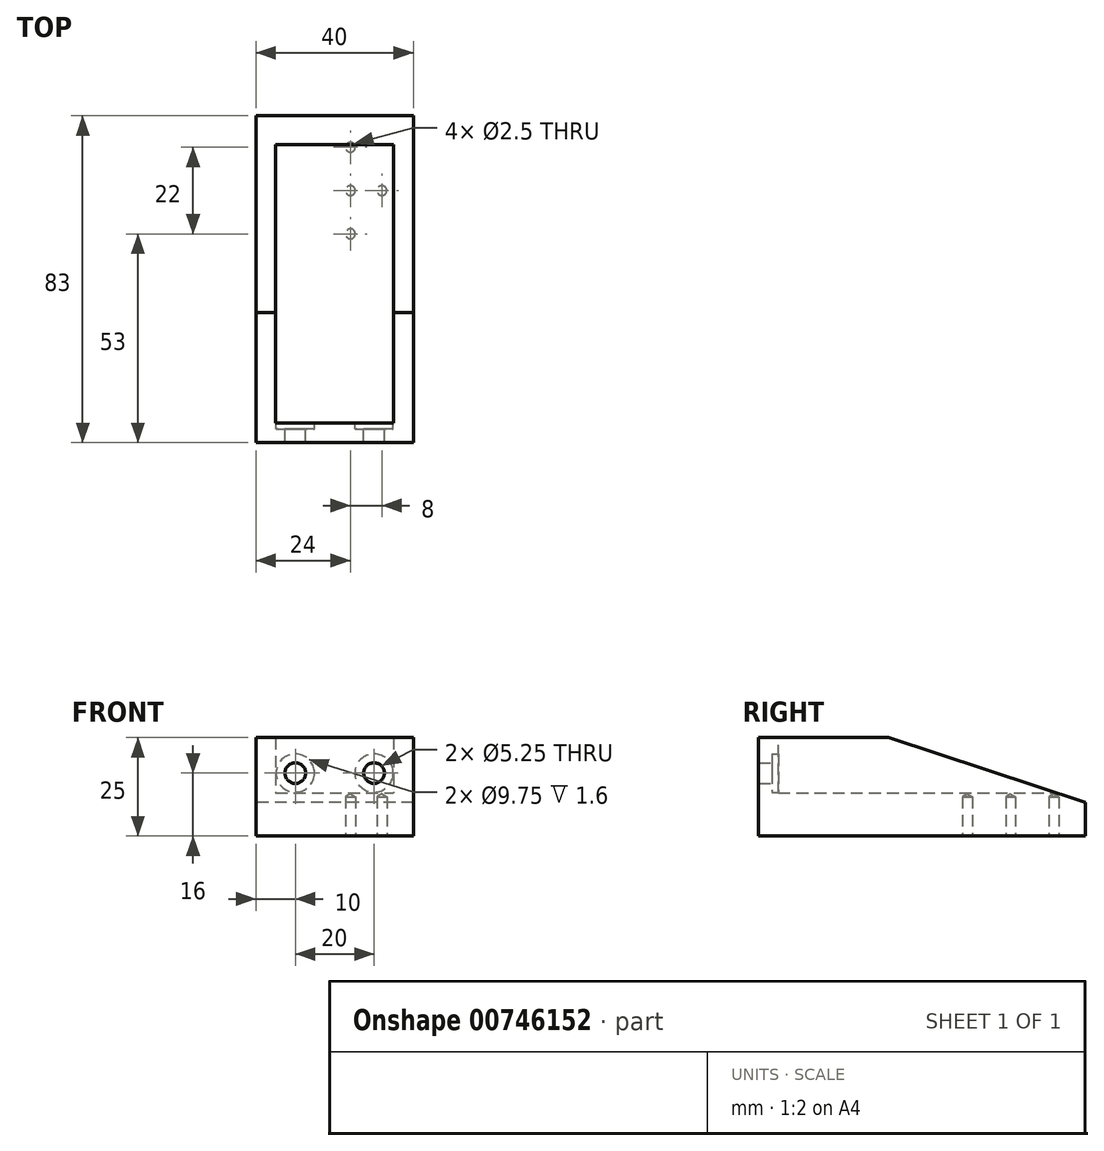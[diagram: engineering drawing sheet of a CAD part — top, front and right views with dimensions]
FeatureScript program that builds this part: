
annotation { "Feature Type Name" : "Feature", "Feature Type Description" : "" }
export const myFeature = defineFeature(function(context is Context, id is Id, definition is map)
    precondition{}
    {
        {
            var Q0;
            Q0=qCreatedBy(makeId("Right.planeOp"),FACE);
            var sketch = newSketch(context, id + "F0", { "sketchPlane" : qUnion([Q0])});
            skLineSegment(sketch, "E0", {"start": v(-78, 0) * mm, "end": v(-78, 16.5) * mm});
            skLineSegment(sketch, "E1", {"start": v(-78, 16.5) * mm, "end": v(-83, 16.5) * mm});
            skLineSegment(sketch, "E2", {"start": v(-83, 16.5) * mm, "end": v(-83, -8.5) * mm});
            skLineSegment(sketch, "E3", {"start": v(-83, -8.5) * mm, "end": v(0, -8.5) * mm});
            skLineSegment(sketch, "E4", {"start": v(0, -8.5) * mm, "end": v(0, 0) * mm});
            skLineSegment(sketch, "E5", {"start": v(0, 0) * mm, "end": v(-78, 0) * mm});
            skLineSegment(sketch, "E6", {"start": v(-78, 16.5) * mm, "end": v(-50, 16.5) * mm});
            skLineSegment(sketch, "E7", {"start": v(-50, 16.5) * mm, "end": v(0, 0) * mm});
            skSolve(sketch);
        }
        {
            var Q0;
            Q0=makeQuery(id+"F0.imprint","IMPRINT",FACE,{"disambiguationData":[TD([[makeQuery(id+"F0.imprint","IMPRINT",EDGE,{"derivedFrom":sQuery(id+"F0.wireOp",EDGE,"E0")}),1.0]])]});
            var Q1;
            {var subQ0=sQuery(id+"F0.wireOp",EDGE,"H235q9Pv-cFfw-opsN-Odyi-TBDRe71CPrCy");Q1=makeQuery(id+"F0.imprint","IMPRINT",FACE,{"disambiguationData":[TD([[makeQuery(id+"F0.imprint","IMPRINT",EDGE,{"derivedFrom":subQ0}),1.0]])]});}
            var Q2;
            Q2=makeQuery(id+"F0.imprint","IMPRINT",FACE,{"disambiguationData":[TD([[makeQuery(id+"F0.imprint","IMPRINT",EDGE,{"derivedFrom":sQuery(id+"F0.wireOp",EDGE,"E0")}),-1.0]])]});
            extrude(context, id + "F1", {"entities" : qUnion([Q0, Q1, Q2]), "depth" : 40 * mm, "offsetDistance" : 25 * mm});
        }
        {
            var Q0;
            Q0=makeQuery(id+"F1.opExtrude","SWEPT_FACE",FACE,{"disambiguationData":[OSD([sQuery(id+"F0.wireOp",EDGE,"E3")])]});
            var sketch = newSketch(context, id + "F2", { "sketchPlane" : qUnion([Q0])});
            skPoint(sketch, "E8", {"position": v(24, 8) * mm});
            skPoint(sketch, "E9", {"position": v(24, 19) * mm});
            skPoint(sketch, "E10", {"position": v(24, 30) * mm});
            skPoint(sketch, "E11", {"position": v(32, 19) * mm});
            skLineSegment(sketch, "E12", {"start": v(32, 83) * mm, "end": v(32, 0) * mm, "construction": true});
            skLineSegment(sketch, "E13", {"start": v(24, 0) * mm, "end": v(24, 83) * mm, "construction": true});
            skLineSegment(sketch, "E14", {"start": v(32, 19) * mm, "end": v(24, 19) * mm});
            skLineSegment(sketch, "E15", {"start": v(24, 8) * mm, "end": v(32, 19) * mm});
            skLineSegment(sketch, "E16", {"start": v(24, 30) * mm, "end": v(32, 19) * mm});
            skLineSegment(sketch, "E17", {"start": v(24, 19) * mm, "end": v(24, 30) * mm});
            skLineSegment(sketch, "E18", {"start": v(24, 19) * mm, "end": v(24, 8) * mm});
            skSolve(sketch);
        }
        {
            var Q0;
            Q0=makeQuery(id+"F1.opExtrude","SWEPT_FACE",FACE,{"disambiguationData":[OSD([sQuery(id+"F0.wireOp",EDGE,"E1"),sQuery(id+"F0.wireOp",EDGE,"E6")])]});
            var sketch = newSketch(context, id + "F3", { "sketchPlane" : qUnion([Q0])});
            skLineSegment(sketch, "E19.bottom", {"start": v(35, -78) * mm, "end": v(5, -78) * mm});
            skLineSegment(sketch, "E19.top", {"start": v(35, -5) * mm, "end": v(5, -5) * mm});
            skLineSegment(sketch, "E19.left", {"start": v(35, -78) * mm, "end": v(35, -5) * mm});
            skLineSegment(sketch, "E19.right", {"start": v(5, -78) * mm, "end": v(5, -5) * mm});
            skSolve(sketch);
        }
        {
            var Q0;
            {var subQ0=sQuery(id+"F3.wireOp",EDGE,"E19.bottom");Q0=makeQuery(id+"F3.imprint","IMPRINT",FACE,{"disambiguationData":[TD([[makeQuery(id+"F3.imprint","IMPRINT",EDGE,{"derivedFrom":subQ0}),-1.0]])]});}
            var Q1;
            {var subQ0=sQuery(id+"F3.wireOp",EDGE,"E19.top");Q1=makeQuery(id+"F3.imprint","IMPRINT",FACE,{"disambiguationData":[TD([[makeQuery(id+"F3.imprint","IMPRINT",EDGE,{"derivedFrom":subQ0}),1.0]])]});}
            extrude(context, id + "F4", {"entities" : qUnion([Q0, Q1]), "operationType" : NewBodyOperationType.REMOVE, "oppositeDirection" : true, "depth" : 14.1 * mm, "offsetDistance" : 25 * mm});
        }
        {
            var Q0;
            Q0=makeQuery(id+"F4.boolean.opBoolean","COPY",FACE,{"derivedFrom":makeQuery(id+"F4.opExtrude","SWEPT_FACE",FACE,{"disambiguationData":[OSD([sQuery(id+"F3.wireOp",EDGE,"E19.bottom")])]})});
            var sketch = newSketch(context, id + "F5", { "sketchPlane" : qUnion([Q0])});
            skPoint(sketch, "E20", {"position": v(-30, 7.5) * mm});
            skPoint(sketch, "E21", {"position": v(-10, 7.5) * mm});
            skSolve(sketch);
        }
        {
            var Q0;
            Q0=sQuery(id+"F5.wireOp",VERTEX,"E20");
            var Q1;
            Q1=sQuery(id+"F5.wireOp",VERTEX,"E21");
            var Q2;
            Q2=makeQuery(id+"F1.opExtrude","SWEPT_BODY",BODY,{"disambiguationData":[OSD([sQuery(id+"F0.wireOp",EDGE,"E1"),sQuery(id+"F0.wireOp",EDGE,"E2"),sQuery(id+"F0.wireOp",EDGE,"E3"),sQuery(id+"F0.wireOp",EDGE,"E4"),sQuery(id+"F0.wireOp",EDGE,"E6"),sQuery(id+"F0.wireOp",EDGE,"E7")])]});
            hole(context, id + "F6", {"style" : HoleStyle.C_BORE, "endStyle" : HoleEndStyle.BLIND, "holeDiameter" : 5.25 * mm, "cBoreDiameter" : 9.75 * mm, "cBoreDepth" : 1.6 * mm, "majorDiameter" : 5 * mm, "holeDepth" : 5 * mm, "isTappedThrough" : true, "tappedDepth" : 12 * mm, "tapClearance" : 3, "startFromSketch" : true, "locations" : qUnion([Q0, Q1]), "scope" : qUnion([Q2])});
        }
        {
            var Q0;
            Q0=sQuery(id+"F2.wireOp",VERTEX,"E10");
            var Q1;
            Q1=sQuery(id+"F2.wireOp",VERTEX,"E9");
            var Q2;
            Q2=sQuery(id+"F2.wireOp",VERTEX,"E14.start");
            var Q3;
            Q3=sQuery(id+"F2.wireOp",VERTEX,"E8");
            var Q4;
            Q4=makeQuery(id+"F1.opExtrude","SWEPT_BODY",BODY,{"disambiguationData":[OSD([sQuery(id+"F0.wireOp",EDGE,"E1"),sQuery(id+"F0.wireOp",EDGE,"E2"),sQuery(id+"F0.wireOp",EDGE,"E3"),sQuery(id+"F0.wireOp",EDGE,"E4"),sQuery(id+"F0.wireOp",EDGE,"E6"),sQuery(id+"F0.wireOp",EDGE,"E7")])]});
            hole(context, id + "F7", {"style" : HoleStyle.SIMPLE, "endStyle" : HoleEndStyle.BLIND, "standardTappedOrClearance" : lookupTablePath({ "standard" : "ISO", "engagement" : "75%", "pitch" : "0.5 mm", "size" : "M3", "type" : "Tapped" }), "standardBlindInLast" : lookupTablePath({ "standard" : "ISO", "engagement" : "75%", "pitch" : "0.5 mm", "size" : "M3", "type" : "Tapped" }), "holeDiameter" : 2.5 * mm, "majorDiameter" : 3 * mm, "showTappedDepth" : true, "holeDepth" : 10 * mm, "isTappedThrough" : true, "tappedDepth" : 10 * mm, "tapClearance" : 0, "startFromSketch" : true, "locations" : qUnion([Q0, Q1, Q2, Q3]), "scope" : qUnion([Q4])});
        }
    });
